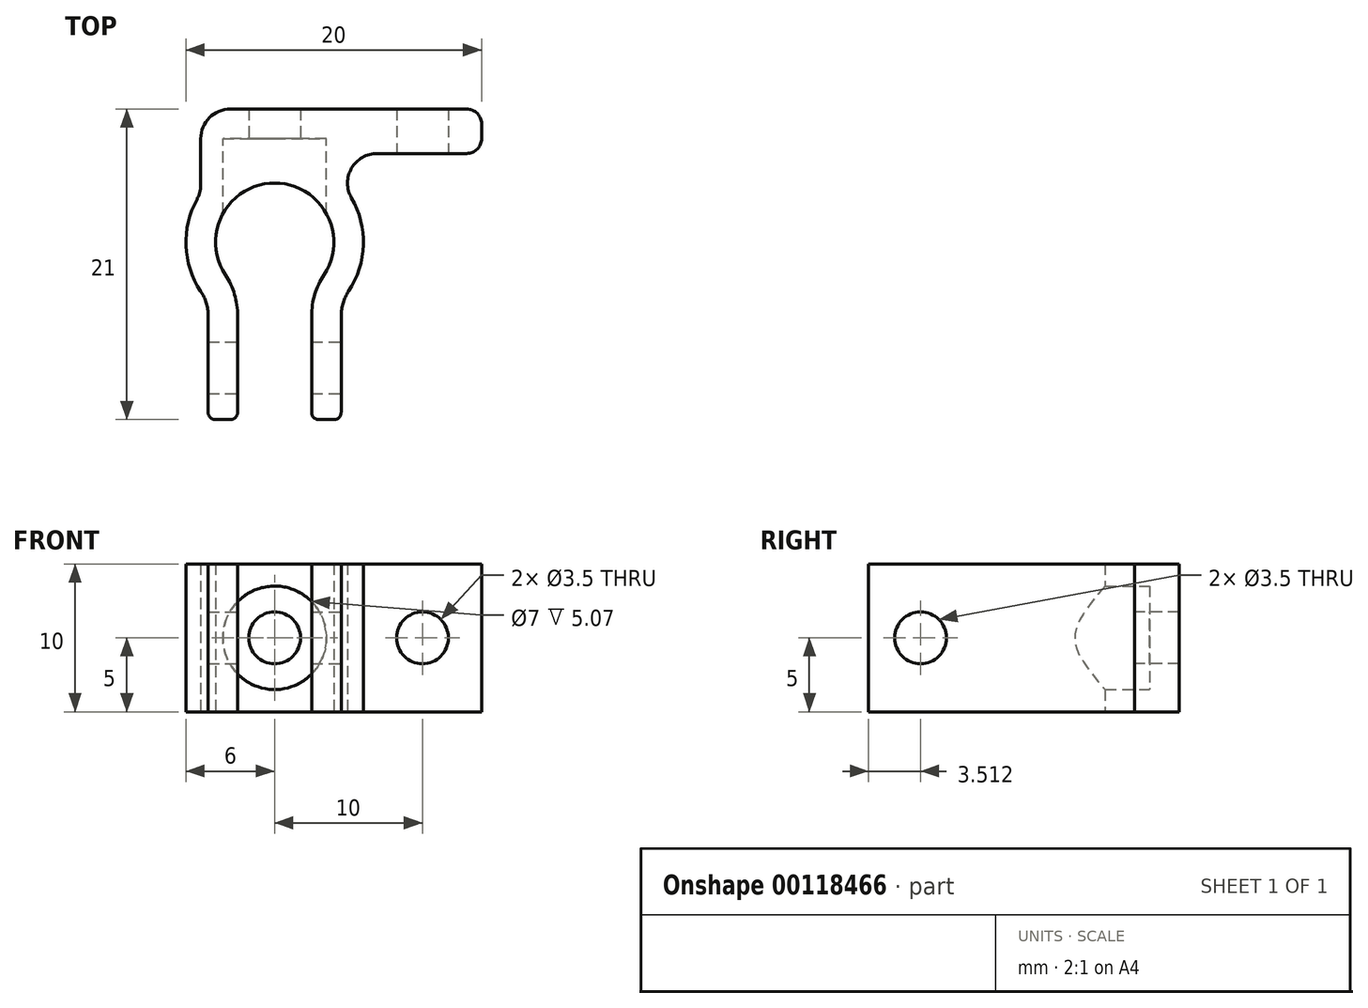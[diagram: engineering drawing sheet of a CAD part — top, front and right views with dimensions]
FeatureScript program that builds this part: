
annotation { "Feature Type Name" : "Feature", "Feature Type Description" : "" }
export const myFeature = defineFeature(function(context is Context, id is Id, definition is map)
    precondition{}
    {
        {
            var Q0;
            Q0=qCreatedBy(makeId("Top.planeOp"),FACE);
            var sketch = newSketch(context, id + "F0", { "sketchPlane" : qUnion([Q0])});
            skLineSegment(sketch, "E0", {"start": v(0, -9) * mm, "end": v(-6, -9) * mm, "construction": true});
            skLineSegment(sketch, "E1", {"start": v(0, -9) * mm, "end": v(6, -9) * mm, "construction": true});
            skLineSegment(sketch, "E2", {"start": v(-4.5, -21) * mm, "end": v(-2.5, -21) * mm});
            skLineSegment(sketch, "E3", {"start": v(4.5, -21) * mm, "end": v(2.5, -21) * mm});
            skLineSegment(sketch, "E4", {"start": v(-2.5, -21) * mm, "end": v(2.5, -21) * mm, "construction": true});
            skLineSegment(sketch, "E5", {"start": v(-2.5, -21) * mm, "end": v(-2.5, -14.45) * mm});
            skLineSegment(sketch, "E6", {"start": v(2.5, -13.97) * mm, "end": v(2.5, -14.45) * mm});
            skLineSegment(sketch, "E7", {"start": v(-4.5, -21) * mm, "end": v(-4.5, -13.97) * mm});
            skLineSegment(sketch, "E8", {"start": v(4.5, -21) * mm, "end": v(4.5, -13.97) * mm});
            skLineSegment(sketch, "E9", {"start": v(-2.5, -14.45) * mm, "end": v(-2.5, -13.97) * mm});
            skLineSegment(sketch, "E10", {"start": v(2.5, -14.45) * mm, "end": v(2.5, -21) * mm});
            skArc(sketch, "E11", {"start": v(-2.5, -12.12) * mm, "mid": v(0, -13) * mm, "end": v(2.5, -12.12) * mm, "construction": true});
            skArc(sketch, "E12", {"start": v(3.33, -11.21) * mm, "mid": v(0, -5) * mm, "end": v(-3.33, -11.21) * mm});
            skArc(sketch, "E13", {"start": v(-4.5, -12.97) * mm, "mid": v(-3.58, -13.82) * mm, "end": v(-2.5, -14.45) * mm, "construction": true});
            skArc(sketch, "E14", {"start": v(-2.5, -14.45) * mm, "mid": v(0, -15) * mm, "end": v(2.5, -14.45) * mm, "construction": true});
            skArc(sketch, "E15", {"start": v(2.5, -14.45) * mm, "mid": v(3.58, -13.82) * mm, "end": v(4.5, -12.97) * mm, "construction": true});
            skArc(sketch, "E16", {"start": v(5, -12.32) * mm, "mid": v(6, -9.19) * mm, "end": v(5.2, -6) * mm});
            skPoint(sketch, "E17.visualSharp", {"position": v(-2.5, -12.12) * mm});
            skArc(sketch, "E17.filletArc", {"start": v(-2.5, -13.97) * mm, "mid": v(-2.71, -12.53) * mm, "end": v(-3.33, -11.21) * mm});
            skPoint(sketch, "E18.visualSharp", {"position": v(2.5, -12.12) * mm});
            skArc(sketch, "E18.filletArc", {"start": v(3.33, -11.21) * mm, "mid": v(2.71, -12.53) * mm, "end": v(2.5, -13.97) * mm});
            skPoint(sketch, "E19", {"position": v(0, -21) * mm});
            skPoint(sketch, "E20.visualSharp", {"position": v(4.5, -12.97) * mm});
            skArc(sketch, "E20.filletArc", {"start": v(5, -12.32) * mm, "mid": v(4.63, -13.1) * mm, "end": v(4.5, -13.97) * mm});
            skPoint(sketch, "E21.visualSharp", {"position": v(-4.5, -12.97) * mm});
            skArc(sketch, "E21.filletArc", {"start": v(-4.5, -13.97) * mm, "mid": v(-4.63, -13.1) * mm, "end": v(-5, -12.32) * mm});
            skLineSegment(sketch, "E22", {"start": v(-5, -5.13) * mm, "end": v(-5, -2) * mm});
            skLineSegment(sketch, "E23", {"start": v(-3, 0) * mm, "end": v(13, 0) * mm});
            skLineSegment(sketch, "E24", {"start": v(14, -1) * mm, "end": v(14, -2) * mm});
            skLineSegment(sketch, "E25", {"start": v(6.93, -3) * mm, "end": v(13, -3) * mm});
            skPoint(sketch, "E26", {"position": v(10, 0) * mm});
            skArc(sketch, "E27", {"start": v(-5.25, -6.1) * mm, "mid": v(-6, -9.24) * mm, "end": v(-5, -12.32) * mm});
            skPoint(sketch, "E28.visualSharp", {"position": v(0, -3) * mm});
            skArc(sketch, "E28.filletArc", {"start": v(6.93, -3) * mm, "mid": v(5.2, -4) * mm, "end": v(5.2, -6) * mm});
            skArc(sketch, "E29.filletArc", {"start": v(-5.25, -6.1) * mm, "mid": v(-5.06, -5.63) * mm, "end": v(-5, -5.13) * mm});
            skPoint(sketch, "E30.visualSharp", {"position": v(14, -3) * mm});
            skArc(sketch, "E30.filletArc", {"start": v(13, -3) * mm, "mid": v(13.7, -2.7) * mm, "end": v(14, -2) * mm});
            skPoint(sketch, "E31.visualSharp", {"position": v(-5, 0) * mm});
            skArc(sketch, "E31.filletArc", {"start": v(-3, 0) * mm, "mid": v(-4.41, -0.59) * mm, "end": v(-5, -2) * mm});
            skPoint(sketch, "E32.visualSharp", {"position": v(14, 0) * mm});
            skArc(sketch, "E32.filletArc", {"start": v(14, -1) * mm, "mid": v(13.7, -0.3) * mm, "end": v(13, 0) * mm});
            skSolve(sketch);
        }
        {
            var Q0;
            Q0=makeQuery(id+"F0.imprint","IMPRINT",FACE,{"disambiguationData":[TD([[makeQuery(id+"F0.imprint","IMPRINT",EDGE,{"derivedFrom":sQuery(id+"F0.wireOp",EDGE,"E2")}),1.0]])]});
            extrude(context, id + "F1", {"entities" : qUnion([Q0]), "depth" : 5 * mm, "hasSecondDirection" : true, "secondDirectionOppositeDirection" : true, "secondDirectionDepth" : 5 * mm});
        }
        {
            var Q0;
            Q0=makeQuery(id+"F1.opExtrude","SWEPT_FACE",FACE,{"disambiguationData":[OSD([sQuery(id+"F0.wireOp",EDGE,"E8")])]});
            cPlane(context, id + "F2", {"entities" : qUnion([Q0]), "cplaneType" : CPlaneType.OFFSET, "offset" : 0 * mm, "width" : 150 * mm, "height" : 150 * mm});
        }
        {
            var Q0;
            Q0=qCreatedBy(id+"F2.planeOp",FACE);
            var sketch = newSketch(context, id + "F3", { "sketchPlane" : qUnion([Q0])});
            skLineSegment(sketch, "E33", {"start": v(-21, 0) * mm, "end": v(-13.97, 0) * mm, "construction": true});
            skPoint(sketch, "E34", {"position": v(-17.49, 0) * mm});
            skSolve(sketch);
        }
        {
            var Q0;
            Q0=sQuery(id+"F3.wireOp",VERTEX,"E34");
            var Q1;
            Q1=makeQuery(id+"F1.opExtrude","SWEPT_BODY",BODY,{"disambiguationData":[OSD([sQuery(id+"F0.wireOp",EDGE,"E2"),sQuery(id+"F0.wireOp",EDGE,"E3"),sQuery(id+"F0.wireOp",EDGE,"E5"),sQuery(id+"F0.wireOp",EDGE,"E6"),sQuery(id+"F0.wireOp",EDGE,"E7"),sQuery(id+"F0.wireOp",EDGE,"E8"),sQuery(id+"F0.wireOp",EDGE,"E9"),sQuery(id+"F0.wireOp",EDGE,"E10"),sQuery(id+"F0.wireOp",EDGE,"E12"),sQuery(id+"F0.wireOp",EDGE,"E16"),sQuery(id+"F0.wireOp",EDGE,"E17.filletArc"),sQuery(id+"F0.wireOp",EDGE,"E18.filletArc"),sQuery(id+"F0.wireOp",EDGE,"E20.filletArc"),sQuery(id+"F0.wireOp",EDGE,"E21.filletArc"),sQuery(id+"F0.wireOp",EDGE,"E22"),sQuery(id+"F0.wireOp",EDGE,"E23"),sQuery(id+"F0.wireOp",EDGE,"E24"),sQuery(id+"F0.wireOp",EDGE,"E25"),sQuery(id+"F0.wireOp",EDGE,"E27"),sQuery(id+"F0.wireOp",EDGE,"E28.filletArc"),sQuery(id+"F0.wireOp",EDGE,"E29.filletArc"),sQuery(id+"F0.wireOp",EDGE,"E30.filletArc")])]});
            hole(context, id + "F4", {"style" : HoleStyle.SIMPLE, "endStyle" : HoleEndStyle.THROUGH, "holeDiameter" : 3.5 * mm, "locations" : qUnion([Q0]), "scope" : qUnion([Q1]), "isTappedThrough" : true});
        }
        {
            var Q0;
            Q0=makeQuery(id+"F1.opExtrude","SWEPT_FACE",FACE,{"disambiguationData":[OSD([sQuery(id+"F0.wireOp",EDGE,"E23")])]});
            cPlane(context, id + "F5", {"entities" : qUnion([Q0]), "cplaneType" : CPlaneType.OFFSET, "offset" : 2 * mm, "oppositeDirection" : true, "width" : 150 * mm, "height" : 150 * mm});
        }
        {
            var Q0;
            Q0=qCreatedBy(id+"F5.planeOp",FACE);
            var sketch = newSketch(context, id + "F6", { "sketchPlane" : qUnion([Q0])});
            skCircle(sketch, "E35", {"center": v(0, 0) * mm, "radius": 3 * mm});
            skPoint(sketch, "E36", {"position": v(-10, 0) * mm});
            skSolve(sketch);
        }
        {
            var Q0;
            Q0=sQuery(id+"F6.wireOp",VERTEX,"E35.center");
            var Q1;
            Q1=sQuery(id+"F6.wireOp",VERTEX,"E36");
            var Q2;
            Q2=makeQuery(id+"F1.opExtrude","SWEPT_BODY",BODY,{"disambiguationData":[OSD([sQuery(id+"F0.wireOp",EDGE,"E2"),sQuery(id+"F0.wireOp",EDGE,"E3"),sQuery(id+"F0.wireOp",EDGE,"E5"),sQuery(id+"F0.wireOp",EDGE,"E6"),sQuery(id+"F0.wireOp",EDGE,"E7"),sQuery(id+"F0.wireOp",EDGE,"E8"),sQuery(id+"F0.wireOp",EDGE,"E9"),sQuery(id+"F0.wireOp",EDGE,"E10"),sQuery(id+"F0.wireOp",EDGE,"E12"),sQuery(id+"F0.wireOp",EDGE,"E16"),sQuery(id+"F0.wireOp",EDGE,"E17.filletArc"),sQuery(id+"F0.wireOp",EDGE,"E18.filletArc"),sQuery(id+"F0.wireOp",EDGE,"E20.filletArc"),sQuery(id+"F0.wireOp",EDGE,"E21.filletArc"),sQuery(id+"F0.wireOp",EDGE,"E22"),sQuery(id+"F0.wireOp",EDGE,"E23"),sQuery(id+"F0.wireOp",EDGE,"E24"),sQuery(id+"F0.wireOp",EDGE,"E25"),sQuery(id+"F0.wireOp",EDGE,"E27"),sQuery(id+"F0.wireOp",EDGE,"E28.filletArc"),sQuery(id+"F0.wireOp",EDGE,"E29.filletArc"),sQuery(id+"F0.wireOp",EDGE,"E30.filletArc")])]});
            hole(context, id + "F7", {"style" : HoleStyle.SIMPLE, "endStyle" : HoleEndStyle.THROUGH, "oppositeDirection" : true, "holeDiameter" : 3.5 * mm, "locations" : qUnion([Q0, Q1]), "scope" : qUnion([Q2]), "isTappedThrough" : true});
        }
        {
            var Q0;
            Q0=sQuery(id+"F6.wireOp",VERTEX,"E36");
            var Q1;
            Q1=makeQuery(id+"F1.opExtrude","SWEPT_BODY",BODY,{"disambiguationData":[OSD([sQuery(id+"F0.wireOp",EDGE,"E2"),sQuery(id+"F0.wireOp",EDGE,"E3"),sQuery(id+"F0.wireOp",EDGE,"E5"),sQuery(id+"F0.wireOp",EDGE,"E6"),sQuery(id+"F0.wireOp",EDGE,"E7"),sQuery(id+"F0.wireOp",EDGE,"E8"),sQuery(id+"F0.wireOp",EDGE,"E9"),sQuery(id+"F0.wireOp",EDGE,"E10"),sQuery(id+"F0.wireOp",EDGE,"E12"),sQuery(id+"F0.wireOp",EDGE,"E16"),sQuery(id+"F0.wireOp",EDGE,"E17.filletArc"),sQuery(id+"F0.wireOp",EDGE,"E18.filletArc"),sQuery(id+"F0.wireOp",EDGE,"E20.filletArc"),sQuery(id+"F0.wireOp",EDGE,"E21.filletArc"),sQuery(id+"F0.wireOp",EDGE,"E22"),sQuery(id+"F0.wireOp",EDGE,"E23"),sQuery(id+"F0.wireOp",EDGE,"E24"),sQuery(id+"F0.wireOp",EDGE,"E25"),sQuery(id+"F0.wireOp",EDGE,"E27"),sQuery(id+"F0.wireOp",EDGE,"E28.filletArc"),sQuery(id+"F0.wireOp",EDGE,"E29.filletArc"),sQuery(id+"F0.wireOp",EDGE,"E30.filletArc")])]});
            hole(context, id + "F8", {"style" : HoleStyle.SIMPLE, "endStyle" : HoleEndStyle.THROUGH, "holeDiameter" : 3.5 * mm, "locations" : qUnion([Q0]), "scope" : qUnion([Q1]), "isTappedThrough" : true});
        }
        {
            var Q0;
            Q0=sQuery(id+"F6.wireOp",VERTEX,"E35.center");
            var Q1;
            Q1=makeQuery(id+"F1.opExtrude","SWEPT_BODY",BODY,{"disambiguationData":[OSD([sQuery(id+"F0.wireOp",EDGE,"E2"),sQuery(id+"F0.wireOp",EDGE,"E3"),sQuery(id+"F0.wireOp",EDGE,"E5"),sQuery(id+"F0.wireOp",EDGE,"E6"),sQuery(id+"F0.wireOp",EDGE,"E7"),sQuery(id+"F0.wireOp",EDGE,"E8"),sQuery(id+"F0.wireOp",EDGE,"E9"),sQuery(id+"F0.wireOp",EDGE,"E10"),sQuery(id+"F0.wireOp",EDGE,"E12"),sQuery(id+"F0.wireOp",EDGE,"E16"),sQuery(id+"F0.wireOp",EDGE,"E17.filletArc"),sQuery(id+"F0.wireOp",EDGE,"E18.filletArc"),sQuery(id+"F0.wireOp",EDGE,"E20.filletArc"),sQuery(id+"F0.wireOp",EDGE,"E21.filletArc"),sQuery(id+"F0.wireOp",EDGE,"E22"),sQuery(id+"F0.wireOp",EDGE,"E23"),sQuery(id+"F0.wireOp",EDGE,"E24"),sQuery(id+"F0.wireOp",EDGE,"E25"),sQuery(id+"F0.wireOp",EDGE,"E27"),sQuery(id+"F0.wireOp",EDGE,"E28.filletArc"),sQuery(id+"F0.wireOp",EDGE,"E29.filletArc"),sQuery(id+"F0.wireOp",EDGE,"E30.filletArc")])]});
            hole(context, id + "F9", {"style" : HoleStyle.SIMPLE, "endStyle" : HoleEndStyle.BLIND, "holeDiameter" : 7 * mm, "holeDepth" : 6 * mm, "locations" : qUnion([Q0]), "scope" : qUnion([Q1])});
        }
        {
            var Q0;
            Q0=makeQuery(id+"F1.opExtrude","SWEPT_EDGE",EDGE,{"disambiguationData":[OSD([sQuery(id+"F0.wireOp",EDGE,"E2"),sQuery(id+"F0.wireOp",EDGE,"E7")])]});
            var Q1;
            Q1=makeQuery(id+"F1.opExtrude","SWEPT_EDGE",EDGE,{"disambiguationData":[OSD([sQuery(id+"F0.wireOp",EDGE,"E2"),sQuery(id+"F0.wireOp",EDGE,"E5")])]});
            var Q2;
            Q2=makeQuery(id+"F1.opExtrude","SWEPT_EDGE",EDGE,{"disambiguationData":[OSD([sQuery(id+"F0.wireOp",EDGE,"E3"),sQuery(id+"F0.wireOp",EDGE,"E10")])]});
            var Q3;
            Q3=makeQuery(id+"F1.opExtrude","SWEPT_EDGE",EDGE,{"disambiguationData":[OSD([sQuery(id+"F0.wireOp",EDGE,"E3"),sQuery(id+"F0.wireOp",EDGE,"E8")])]});
            var Q4;
            Q4=makeQuery(id+"F9.hole-0.boolean.opBoolean","INTERSECT",EDGE,{"derivedFrom":[makeQuery(id+"F1.opExtrude","SWEPT_FACE",FACE,{"disambiguationData":[OSD([sQuery(id+"F0.wireOp",EDGE,"E12")])]}),makeQuery(id+"F9.hole-0.opRevolve","SWEPT_FACE",FACE,{"disambiguationData":[OSD([sQuery(id+"F9.hole-0.sketch.wireOp",EDGE,"core_line_2")])]})]});
            fillet(context, id + "F10", {"entities" : qUnion([Q0, Q1, Q2, Q3, Q4]), "radius" : 0.5 * mm, "tangentPropagation" : true, "allowEdgeOverflow" : false});
        }
    });
